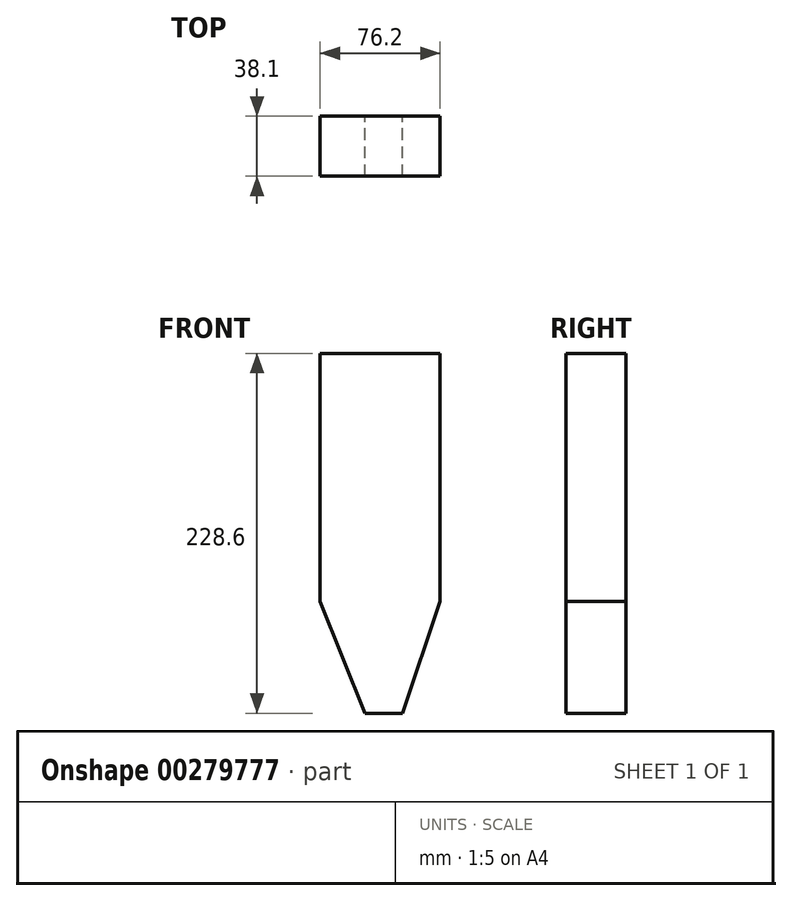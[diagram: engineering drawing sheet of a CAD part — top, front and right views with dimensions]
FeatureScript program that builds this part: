
annotation { "Feature Type Name" : "Feature", "Feature Type Description" : "" }
export const myFeature = defineFeature(function(context is Context, id is Id, definition is map)
    precondition{}
    {
        {
            var Q0;
            Q0=qCreatedBy(makeId("Front.planeOp"),FACE);
            var sketch = newSketch(context, id + "F0", { "sketchPlane" : qUnion([Q0])});
            skLineSegment(sketch, "E0.bottom", {"start": v(-38.78, 187.54) * mm, "end": v(37.42, 187.54) * mm});
            skLineSegment(sketch, "E0.top", {"start": v(-10.43, -41.06) * mm, "end": v(13.48, -41.06) * mm});
            skLineSegment(sketch, "E0.left", {"start": v(-38.78, 187.54) * mm, "end": v(-38.78, 29.83) * mm});
            skLineSegment(sketch, "E0.right", {"start": v(37.42, 187.54) * mm, "end": v(37.42, 29.83) * mm});
            skLineSegment(sketch, "E1", {"start": v(-10.43, -41.06) * mm, "end": v(-38.78, 29.83) * mm});
            skLineSegment(sketch, "E2", {"start": v(13.48, -41.06) * mm, "end": v(37.42, 29.83) * mm});
            skSolve(sketch);
        }
        {
            var Q0;
            Q0 = qSketchRegion(id + "F0", true);
            extrude(context, id + "F1", {"entities" : qUnion([Q0]), "depth" : 38.1 * mm});
        }
    });
